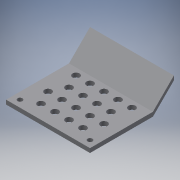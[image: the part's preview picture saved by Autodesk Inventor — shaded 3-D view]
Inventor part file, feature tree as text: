
AUTODESK INVENTOR PART (.ipt)
format: ipt  version: 2016 (Build 200138000, 138)  size: 161,280 bytes
history: native  units: mm
features: extrude x3, sketch x3, projected_geometry x2
ambient origin geometry x8: Origin, YZ Plane, XZ Plane, XY Plane, X Axis, Y Axis, Z Axis, Center Point
bodies: Body1 (feature_tree)
feature tree (8):
  extrude  "Extrusion3"  TaperAngle=135.0deg  [1 undecoded]
  extrude  "Extrusion4"  Depth=45.0mm
  extrude  "Extrusion5"  Depth=3.0mm
  sketch  "Sketch3"  dims[d7=45.0mm d8=135.0deg]
  sketch  "Sketch4"  dims[d10=15.0mm d11=45.0mm]
  projected_geometry  "Projected Loop1"
  sketch  "Sketch5"  dims[d12=21.213203mm d13=3.0mm d14=60.0mm d15=0.0mm d16=3.5mm d18=50.0mm d19=5.0mm d20=60.0mm d21=0.0mm d22=5.0mm d23=50.0mm d25=10.0mm d26=20.0mm d28=20.0mm d32=5.0mm d33=10.0mm d35=10.0mm d36=40.0mm d38=10.0mm d39=20.0mm d41=20.0mm d44=60.0mm d45=0.0mm]
  projected_geometry  "Projected Loop2"
note: 1 required parameter value undecoded (feature->parameter linkage not recoverable at this tier; creation-order binding heuristic only, values carry confidence <= 0.55)
